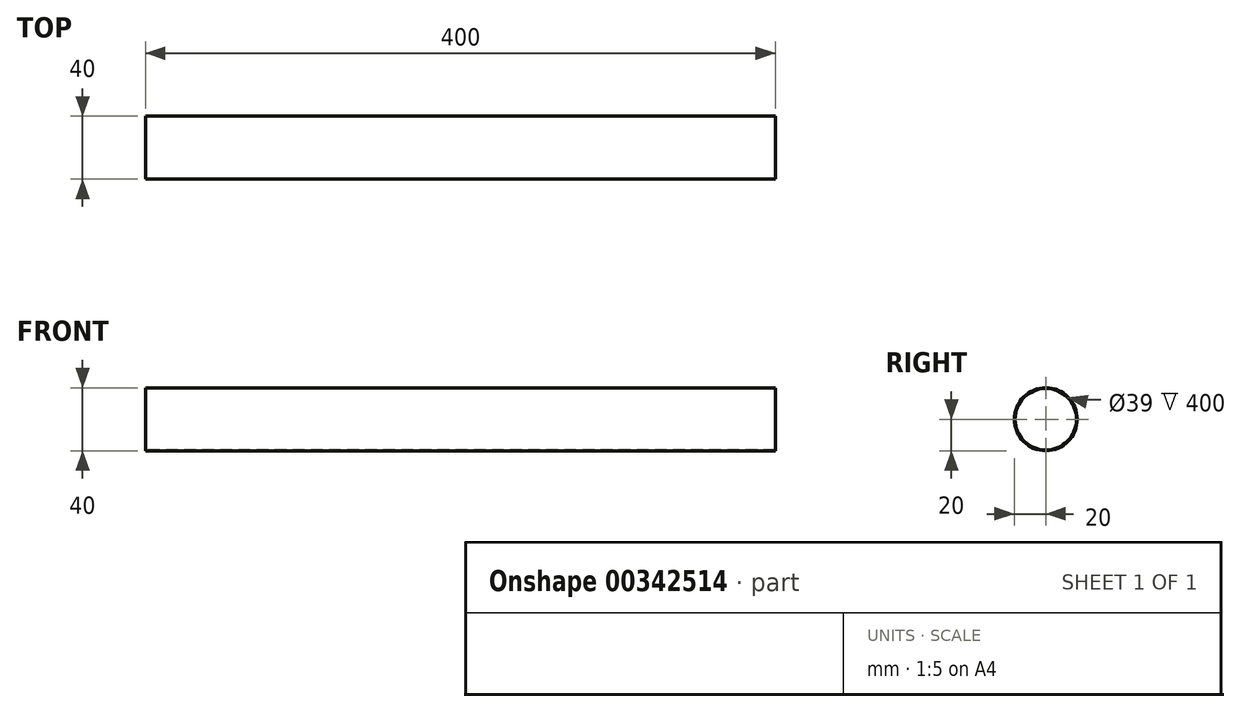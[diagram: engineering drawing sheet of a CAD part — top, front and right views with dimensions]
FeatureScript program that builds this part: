
annotation { "Feature Type Name" : "Feature", "Feature Type Description" : "" }
export const myFeature = defineFeature(function(context is Context, id is Id, definition is map)
    precondition{}
    {
        {
            var Q0;
            Q0=qCreatedBy(makeId("Right.planeOp"),FACE);
            var sketch = newSketch(context, id + "F0", { "sketchPlane" : qUnion([Q0])});
            skCircle(sketch, "E0", {"center": v(0, 0) * mm, "radius": 20 * mm});
            skCircle(sketch, "E1", {"center": v(0, 0) * mm, "radius": 19.5 * mm});
            skSolve(sketch);
        }
        {
            var Q0;
            Q0=makeQuery(id+"F0.imprint","IMPRINT",FACE,{"disambiguationData":[TD([[makeQuery(id+"F0.imprint","IMPRINT",EDGE,{"derivedFrom":sQuery(id+"F0.wireOp",EDGE,"E0")}),1.0]])]});
            extrude(context, id + "F1", {"entities" : qUnion([Q0]), "depth" : 400 * mm});
        }
    });
